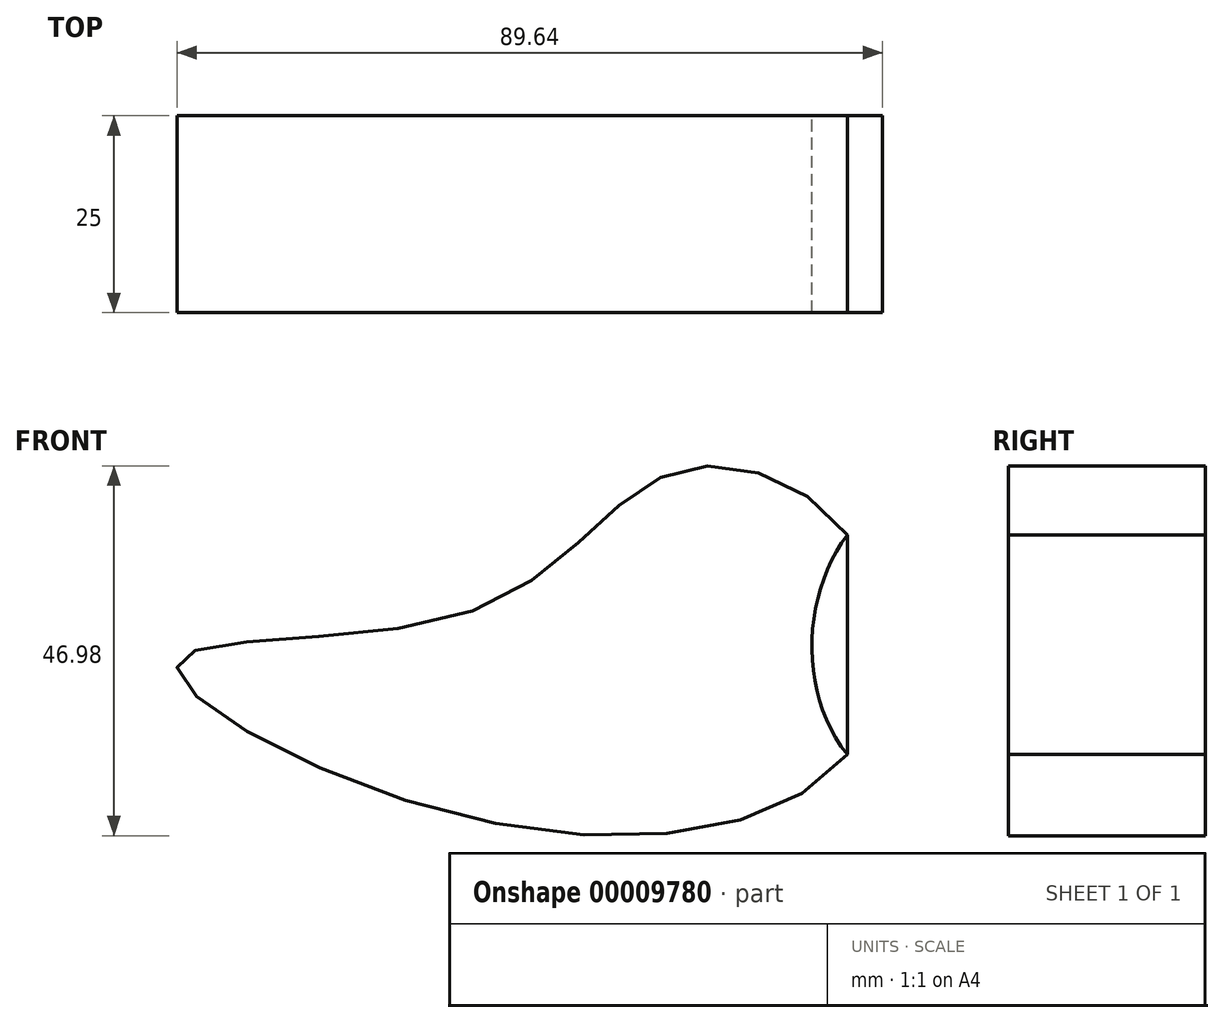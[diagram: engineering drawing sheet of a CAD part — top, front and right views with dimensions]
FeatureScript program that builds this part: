
annotation { "Feature Type Name" : "Feature", "Feature Type Description" : "" }
export const myFeature = defineFeature(function(context is Context, id is Id, definition is map)
    precondition{}
    {
        {
            var Q0;
            Q0=qCreatedBy(makeId("Front.planeOp"),FACE);
            var sketch = newSketch(context, id + "F0", { "sketchPlane" : qUnion([Q0])});
            skFitSpline(sketch, "E0", {"points": [v(0, 21.76) * mm, v(-22.16, 29.71) * mm, v(-47.18, 12.25) * mm, v(-84.97, 5.73) * mm, v(-49.52, -13.81) * mm, v(0, -6.12) * mm, v(0, 21.76) * mm]});
            skLineSegment(sketch, "E1", {"start": v(0, 21.76) * mm, "end": v(0, -6.12) * mm});
            skFitSpline(sketch, "E2.0.MirrorCS", {"points": [v(0, 21.76) * mm, v(22.16, 29.71) * mm, v(47.18, 12.25) * mm, v(84.97, 5.73) * mm, v(49.52, -13.81) * mm, v(0, -6.12) * mm, v(0, 21.76) * mm]});
            skSolve(sketch);
        }
        {
            var Q0;
            Q0=makeQuery(id+"F0.imprint","IMPRINT",FACE,{"disambiguationData":[TD([[makeQuery(id+"F0.imprint","IMPRINT",EDGE,{"derivedFrom":sQuery(id+"F0.wireOp",EDGE,"E0")}),1.0]])]});
            var Q1;
            Q1=makeQuery(id+"F0.imprint","IMPRINT",FACE,{"disambiguationData":[TD([[makeQuery(id+"F0.imprint","IMPRINT",EDGE,{"derivedFrom":sQuery(id+"F0.wireOp",EDGE,"E1")}),1.0]])]});
            extrude(context, id + "F1", {"entities" : qUnion([Q0, Q1]), "depth" : 25 * mm});
        }
    });
